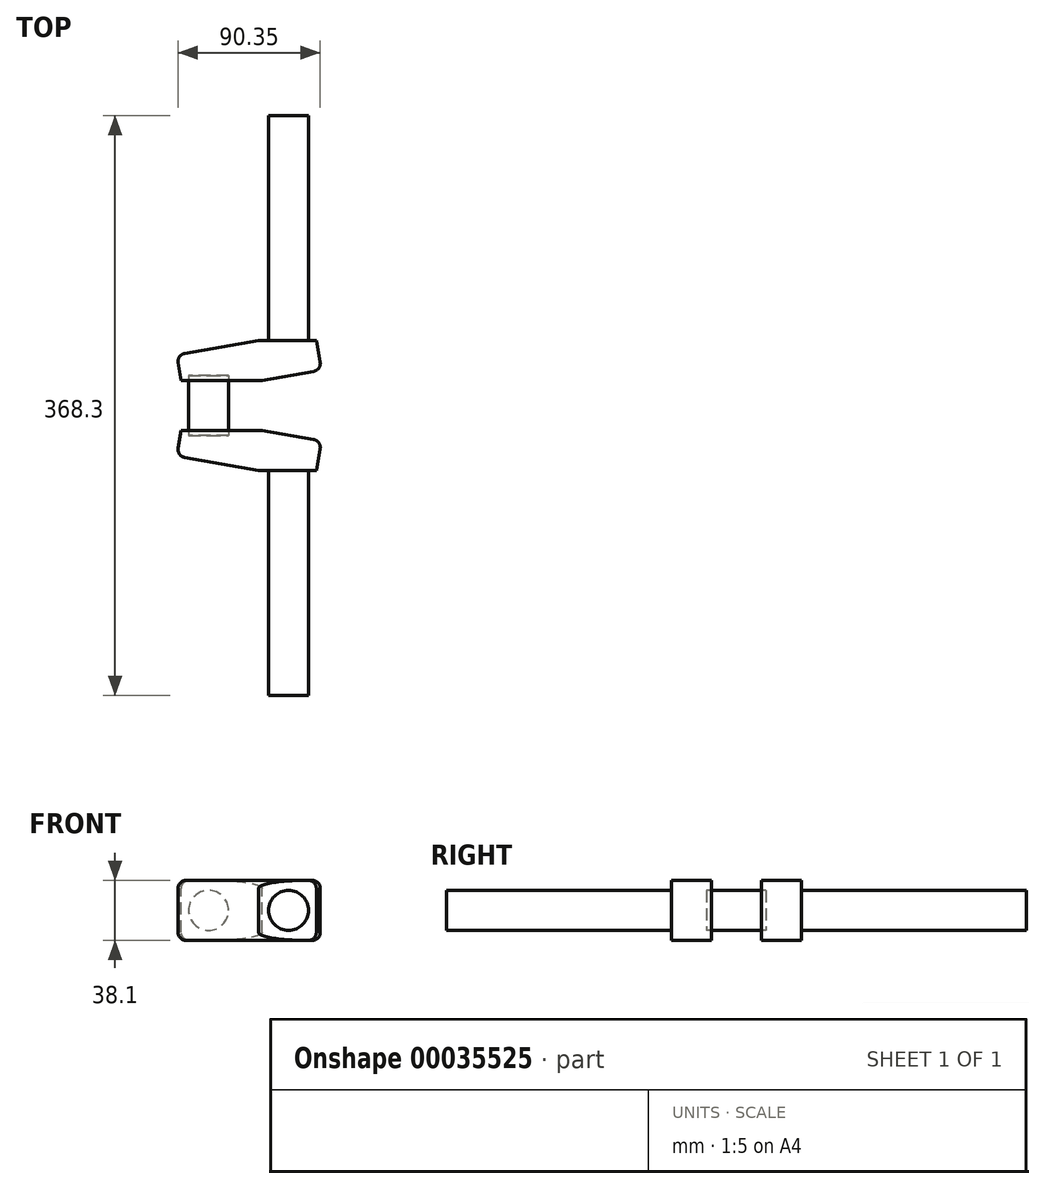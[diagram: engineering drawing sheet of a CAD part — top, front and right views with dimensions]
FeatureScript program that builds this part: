
annotation { "Feature Type Name" : "Feature", "Feature Type Description" : "" }
export const myFeature = defineFeature(function(context is Context, id is Id, definition is map)
    precondition{}
    {
        {
            var Q0;
            Q0=qCreatedBy(makeId("Front.planeOp"),FACE);
            var sketch = newSketch(context, id + "F0", { "sketchPlane" : qUnion([Q0])});
            skCircle(sketch, "E0", {"center": v(0, 0) * mm, "radius": 12.7 * mm});
            skLineSegment(sketch, "E1", {"start": v(0, 25.07) * mm, "end": v(0, -31.2) * mm, "construction": true});
            skSolve(sketch);
        }
        {
            var Q0;
            Q0 = qSketchRegion(id + "F0", true);
            extrude(context, id + "F1", {"entities" : qUnion([Q0]), "oppositeDirection" : true, "depth" : 152.4 * mm});
        }
        {
            var Q0;
            Q0=sQuery(id+"F0.wireOp",EDGE,"E1");
            var Q1;
            Q1=makeQuery(id+"F0.imprint","IMPRINT",FACE,{"disambiguationData":[TD([[makeQuery(id+"F0.imprint","IMPRINT",EDGE,{"derivedFrom":sQuery(id+"F0.wireOp",EDGE,"E0")}),1.0]])]});
            cPlane(context, id + "F2", {"entities" : qUnion([Q0, Q1]), "cplaneType" : CPlaneType.LINE_ANGLE, "offset" : 25.4 * mm, "angle" : 170 * degree, "width" : 152.4 * mm, "height" : 152.4 * mm});
        }
        {
            var Q0;
            Q0=qCreatedBy(id+"F2.planeOp",FACE);
            var sketch = newSketch(context, id + "F3", { "sketchPlane" : qUnion([Q0])});
            skLineSegment(sketch, "E2.bottom", {"start": v(19.05, 19.05) * mm, "end": v(-69.85, 19.05) * mm});
            skLineSegment(sketch, "E2.top", {"start": v(19.05, -19.05) * mm, "end": v(-69.85, -19.05) * mm});
            skLineSegment(sketch, "E2.left", {"start": v(19.05, 19.05) * mm, "end": v(19.05, -19.05) * mm});
            skLineSegment(sketch, "E2.right", {"start": v(-69.85, 19.05) * mm, "end": v(-69.85, -19.05) * mm});
            skSolve(sketch);
        }
        {
            var Q0;
            Q0 = qSketchRegion(id + "F3", true);
            extrude(context, id + "F4", {"entities" : qUnion([Q0]), "operationType" : NewBodyOperationType.ADD, "depth" : 25.4 * mm, "symmetric" : true});
        }
        {
            var Q0;
            Q0=makeQuery(id+"F4.opExtrude","SWEPT_FACE",FACE,{"disambiguationData":[OSD([sQuery(id+"F3.wireOp",EDGE,"E2.bottom")])]});
            var Q1;
            Q1=makeQuery(id+"F4.opExtrude","SWEPT_FACE",FACE,{"disambiguationData":[OSD([sQuery(id+"F3.wireOp",EDGE,"E2.top")])]});
            var Q2;
            Q2=makeQuery(id+"F4.opExtrude","SWEPT_FACE",FACE,{"disambiguationData":[OSD([sQuery(id+"F3.wireOp",EDGE,"E2.right")])]});
            var Q3;
            Q3=makeQuery(id+"F4.opExtrude","SWEPT_FACE",FACE,{"disambiguationData":[OSD([sQuery(id+"F3.wireOp",EDGE,"E2.left")])]});
            fillet(context, id + "F5", {"entities" : qUnion([Q0, Q1, Q2, Q3]), "radius" : 5.08 * mm, "tangentPropagation" : true, "allowEdgeOverflow" : false});
        }
        {
            var Q0;
            Q0=qCreatedBy(makeId("Front.planeOp"),FACE);
            var sketch = newSketch(context, id + "F6", { "sketchPlane" : qUnion([Q0])});
            skCircle(sketch, "E3", {"center": v(0, 0) * mm, "radius": 30.94 * mm});
            skCircle(sketch, "E4", {"center": v(0, 0) * mm, "radius": 12.7 * mm});
            skSolve(sketch);
        }
        {
            var Q0;
            Q0 = qSketchRegion(id + "F6", true);
            extrude(context, id + "F7", {"entities" : qUnion([Q0]), "oppositeDirection" : true, "depth" : 25.4 * mm});
        }
        {
            var Q0;
            Q0=makeQuery(id+"F7.opExtrude","SWEPT_BODY",BODY,{"disambiguationData":[OSD([sQuery(id+"F6.wireOp",EDGE,"E3"),sQuery(id+"F6.wireOp",EDGE,"E4")])]});
            var Q1;
            Q1=makeQuery(id+"F1.opExtrude","CAP_EDGE",EDGE,{"disambiguationData":[OSD([sQuery(id+"F0.wireOp",EDGE,"E0")])],"isStart":false});
            transform(context, id + "F8", {"entities" : qUnion([Q0]), "transformType" : TransformType.TRANSLATION_3D, "dx" : 0 * mm, "dy" : 9.52 * mm, "dz" : 0 * mm, "makeCopy" : false});
        }
        {
            var Q0;
            Q0=makeQuery(id+"F7.opExtrude","SWEPT_BODY",BODY,{"disambiguationData":[OSD([sQuery(id+"F6.wireOp",EDGE,"E3"),sQuery(id+"F6.wireOp",EDGE,"E4")])]});
            var Q1;
            Q1=makeQuery(id+"F1.opExtrude","SWEPT_BODY",BODY,{"disambiguationData":[OSD([sQuery(id+"F0.wireOp",EDGE,"E0")])]});
            booleanBodies(context, id + "F9", {"operationType" : BooleanOperationType.SUBTRACTION, "tools" : qUnion([Q0]), "targets" : qUnion([Q1])});
        }
        {
            var Q0;
            Q0=makeQuery(id+"F1.opExtrude","SWEPT_BODY",BODY,{"disambiguationData":[OSD([sQuery(id+"F0.wireOp",EDGE,"E0")])]});
            var Q1;
            Q1=qCreatedBy(makeId("Front.planeOp"),FACE);
            mirror(context, id + "F10", {"entities" : qUnion([Q0]), "mirrorPlane" : qUnion([Q1])});
        }
        {
            var Q0;
            Q0=makeQuery(id+"F10.opPattern","COPY",BODY,{"derivedFrom":makeQuery(id+"F1.opExtrude","SWEPT_BODY",BODY,{"disambiguationData":[OSD([sQuery(id+"F0.wireOp",EDGE,"E0")])]}),"instanceName":"1"});
            transform(context, id + "F11", {"entities" : qUnion([Q0]), "transformType" : TransformType.TRANSLATION_3D, "dx" : 0 * mm, "dy" : -63.5 * mm, "dz" : 0 * mm, "makeCopy" : false});
        }
        {
            var Q0;
            Q0=makeQuery(id+"F1.opExtrude","CAP_FACE",FACE,{"disambiguationData":[OSD([sQuery(id+"F0.wireOp",EDGE,"E0")])],"isStart":false});
            var Q1;
            Q1=makeQuery(id+"F10.opPattern","COPY",FACE,{"derivedFrom":makeQuery(id+"F1.opExtrude","CAP_FACE",FACE,{"disambiguationData":[OSD([sQuery(id+"F0.wireOp",EDGE,"E0")])],"isStart":false}),"instanceName":"1"});
            cPlane(context, id + "F12", {"entities" : qUnion([Q0, Q1]), "cplaneType" : CPlaneType.MID_PLANE, "offset" : 25.4 * mm, "width" : 152.4 * mm, "height" : 152.4 * mm});
        }
        {
            var Q0;
            Q0=qCreatedBy(id+"F12.planeOp",FACE);
            var sketch = newSketch(context, id + "F13", { "sketchPlane" : qUnion([Q0])});
            skLineSegment(sketch, "E5.bottom", {"start": v(70.13, 24.22) * mm, "end": v(9.06, 24.22) * mm});
            skLineSegment(sketch, "E5.top", {"start": v(70.13, -25.26) * mm, "end": v(9.06, -25.26) * mm});
            skLineSegment(sketch, "E5.left", {"start": v(70.13, 24.22) * mm, "end": v(70.13, -25.26) * mm});
            skLineSegment(sketch, "E5.right", {"start": v(9.06, 24.22) * mm, "end": v(9.06, -25.26) * mm});
            skSolve(sketch);
        }
        {
            var Q0;
            Q0 = qSketchRegion(id + "F13", true);
            extrude(context, id + "F14", {"entities" : qUnion([Q0]), "depth" : 31.75 * mm, "symmetric" : true});
        }
        {
            var Q0;
            Q0=makeQuery(id+"F14.opExtrude","SWEPT_BODY",BODY,{"disambiguationData":[OSD([sQuery(id+"F13.wireOp",EDGE,"E5.bottom"),sQuery(id+"F13.wireOp",EDGE,"E5.top"),sQuery(id+"F13.wireOp",EDGE,"E5.left"),sQuery(id+"F13.wireOp",EDGE,"E5.right")])]});
            var Q1;
            Q1=makeQuery(id+"F1.opExtrude","SWEPT_BODY",BODY,{"disambiguationData":[OSD([sQuery(id+"F0.wireOp",EDGE,"E0")])]});
            var Q2;
            Q2=makeQuery(id+"F10.opPattern","COPY",BODY,{"derivedFrom":makeQuery(id+"F1.opExtrude","SWEPT_BODY",BODY,{"disambiguationData":[OSD([sQuery(id+"F0.wireOp",EDGE,"E0")])]}),"instanceName":"1"});
            booleanBodies(context, id + "F15", {"operationType" : BooleanOperationType.SUBTRACTION, "tools" : qUnion([Q0]), "targets" : qUnion([Q1, Q2])});
        }
        {
            var Q0;
            Q0=qCreatedBy(id+"F12.planeOp",FACE);
            var sketch = newSketch(context, id + "F16", { "sketchPlane" : qUnion([Q0])});
            skCircle(sketch, "E6", {"center": v(50.8, 0) * mm, "radius": 12.7 * mm});
            skSolve(sketch);
        }
        {
            var Q0;
            Q0=makeQuery(id+"F16.imprint","IMPRINT",FACE,{"disambiguationData":[TD([[makeQuery(id+"F16.imprint","IMPRINT",EDGE,{"derivedFrom":sQuery(id+"F16.wireOp",EDGE,"E6")}),1.0]])]});
            var Q1;
            Q1=sQuery(id+"F16.wireOp",EDGE,"E6");
            extrude(context, id + "F17", {"entities" : qUnion([Q0]), "surfaceEntities" : qUnion([Q1]), "depth" : 38.1 * mm, "symmetric" : true});
        }
    });
